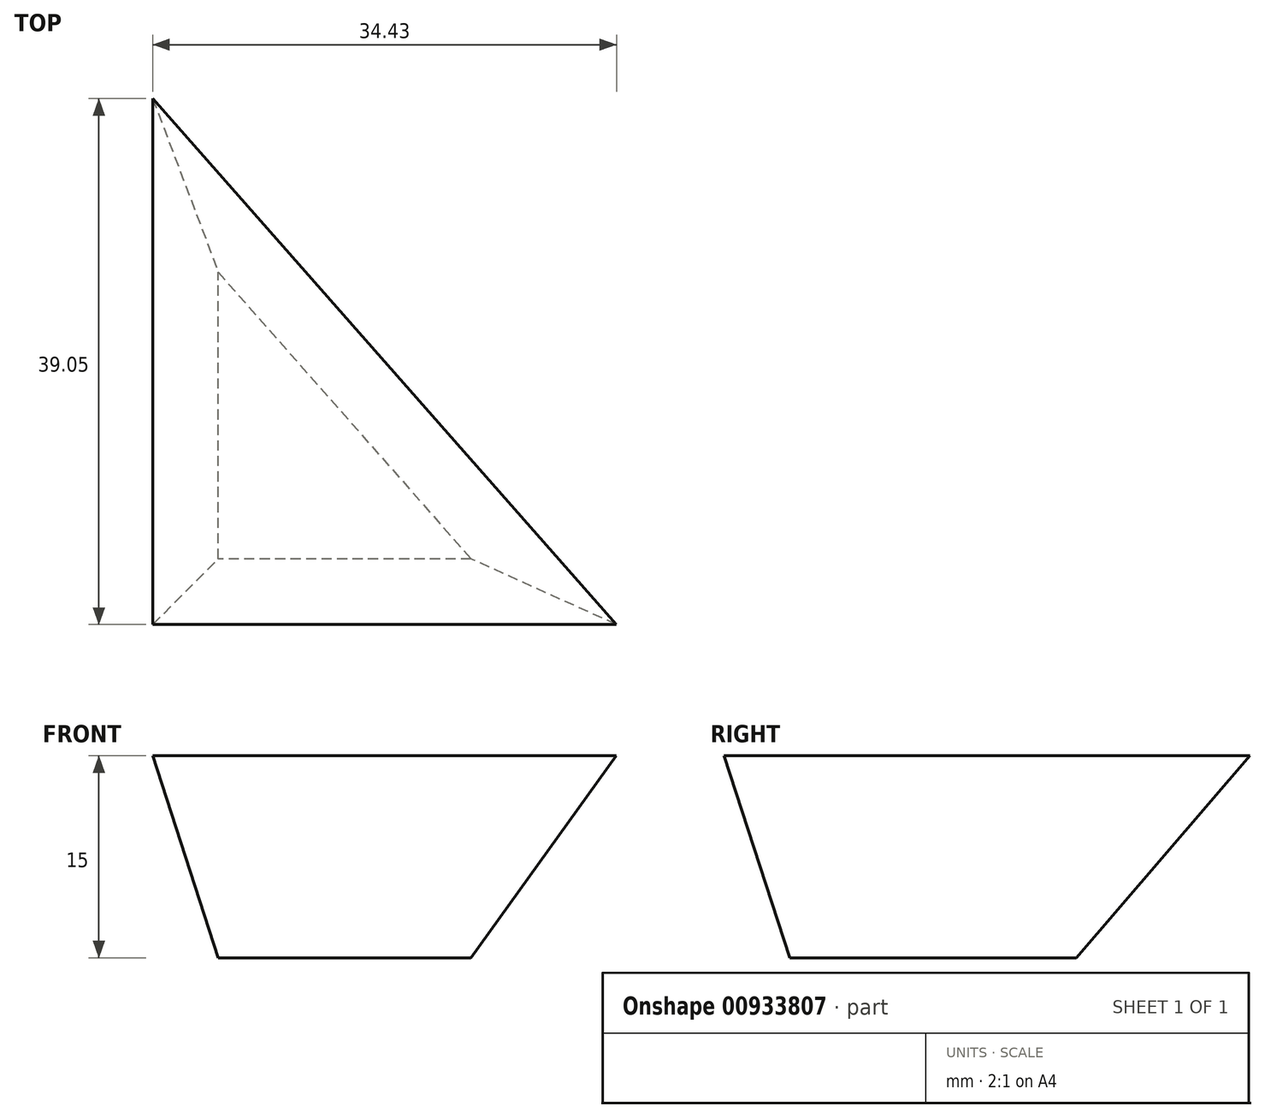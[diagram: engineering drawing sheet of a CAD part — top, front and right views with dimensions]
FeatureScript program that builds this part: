
annotation { "Feature Type Name" : "Feature", "Feature Type Description" : "" }
export const myFeature = defineFeature(function(context is Context, id is Id, definition is map)
    precondition{}
    {
        {
            var Q0;
            Q0=qCreatedBy(makeId("Top.planeOp"),FACE);
            var sketch = newSketch(context, id + "F0", { "sketchPlane" : qUnion([Q0])});
            skLineSegment(sketch, "E0", {"start": v(-18.74, 0) * mm, "end": v(18.76, 0) * mm, "construction": true});
            skLineSegment(sketch, "E1", {"start": v(0, 0) * mm, "end": v(0, 21.28) * mm});
            skLineSegment(sketch, "E2", {"start": v(0, 21.28) * mm, "end": v(-18.74, 0) * mm});
            skLineSegment(sketch, "E3", {"start": v(0, 21.28) * mm, "end": v(18.76, 0) * mm});
            skLineSegment(sketch, "E4", {"start": v(17.04, 0) * mm, "end": v(-18.74, 0) * mm});
            skLineSegment(sketch, "E5", {"start": v(17.04, 0) * mm, "end": v(18.76, 0) * mm});
            skSolve(sketch);
        }
        {
            var Q0;
            {var subQ0=sQuery(id+"F0.wireOp",EDGE,"E1");Q0=makeQuery(id+"F0.imprint","IMPRINT",FACE,{"disambiguationData":[TD([[makeQuery(id+"F0.imprint","IMPRINT",EDGE,{"derivedFrom":subQ0}),-1.0]])]});}
            extrude(context, id + "F1", {"entities" : qUnion([Q0]), "depth" : 15 * mm, "offsetDistance" : 25 * mm, "hasDraft" : true, "draftAngle" : 18 * degree});
        }
    });
